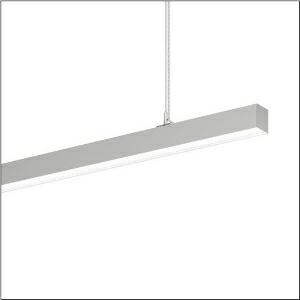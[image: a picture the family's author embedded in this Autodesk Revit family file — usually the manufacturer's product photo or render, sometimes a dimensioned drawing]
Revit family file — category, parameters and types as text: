
# Revit family: silica_r__21_51mx33da47sb_3209
name_source: partatom
category: Lighting Fixtures
units: mm (PartAtom-declared; Revit-internal decimal feet)

## family parameters
Cut with Voids When Loaded = No
Host = Face
Light Source = No
Part Type = Normal
Room Calculation Point = No
Round Connector Dimension = Use Diameter
Shared = No

## types (1)
- --- (1 x LED, 5910 lm, 38.4 W, 4000K)
    Apparent Load = 38 VA
    CIE Flux Codes = 78 96 99 55 100
    Color Rendering = 80
    Color Temperature = 4000K
    Default Elevation = 1800 mm
    Description = Silica® 21, office luminaire, primary optical cover: prismatic diffuser, of PMMA, CAT 2 (L<= 3000cd/m²), light emission: direct/indirect distribution, primary light characteristic: symmetric, installation type: suspended mounting, LED, rated luminous flux: 5.910lm, luminous efficacy: 154lm/W, light colour: 840, colour temperature: 4000K, control gear: DALI 2, with terminal, 3+2-pole, max. 2.5mm², mains connection: 220..240V, AC, 50/60Hz, rated input power: 38.4W, luminaire housing, of aluminium, metallic grey (RAL 9006), length: 1.204mm, width: 53mm, height: 53mm, protection rating (complete): IP20, insulation class (complete): insulation class I (protective earthing), certification: CE, permissible operating ambient temperature: 0..+35°C, standard: EN 50419, packaging unit: 1 piece
    Height = 53 mm
    Lamp = 1 x LED
    Lamp Light Flux = 5910 lm
    Lamp Power = 38.4 W
    Lamp count = 1
    Length = 1204 mm
    Luminous efficacy = 154 lm/W
    Manufacturer = Siteco
    ModVariant = No
    Model = 51MX33DA47SB
    Mounting Place = Ceiling
    Mounting Type = Pendant
    Number of Poles = 1
    OnlyDefault = Yes
    Power Factor = 1
    Product Name = Silica® 21
    Product group = office luminaire | ceiling pendant
    ProductGroupID = 904
    Protection Class = Protection class I
    Protection Degree = IP 20
    RLX_Detail_Level = 1
    RLX_Emergency_Light_Flux = 0 lm
    RLX_Emergency_Type = 0
    RLX_Emergency_Type_DB = No
    RlxData = <blob elided: 23141 chars, md5=e76e480f>
    Socket = socket
    Standby Power = 0 W
    System Light Flux = 5910 lm
    System Power = 38 W
    Type Comments = factory setting: luminous flux: 100 % | dim-lin: 254 | 322 mA
    Type Image = l_1335864.jpg
    URL = http://relux.com
    VarID = @adj_118588
    Voltage = 0 V
    Weight = 0.00 kg
    Width = 53 mm

## geometry (parser evidence)
native form markers: Blend x4, Sweep x11
no freeform markers — native parametric forms only
